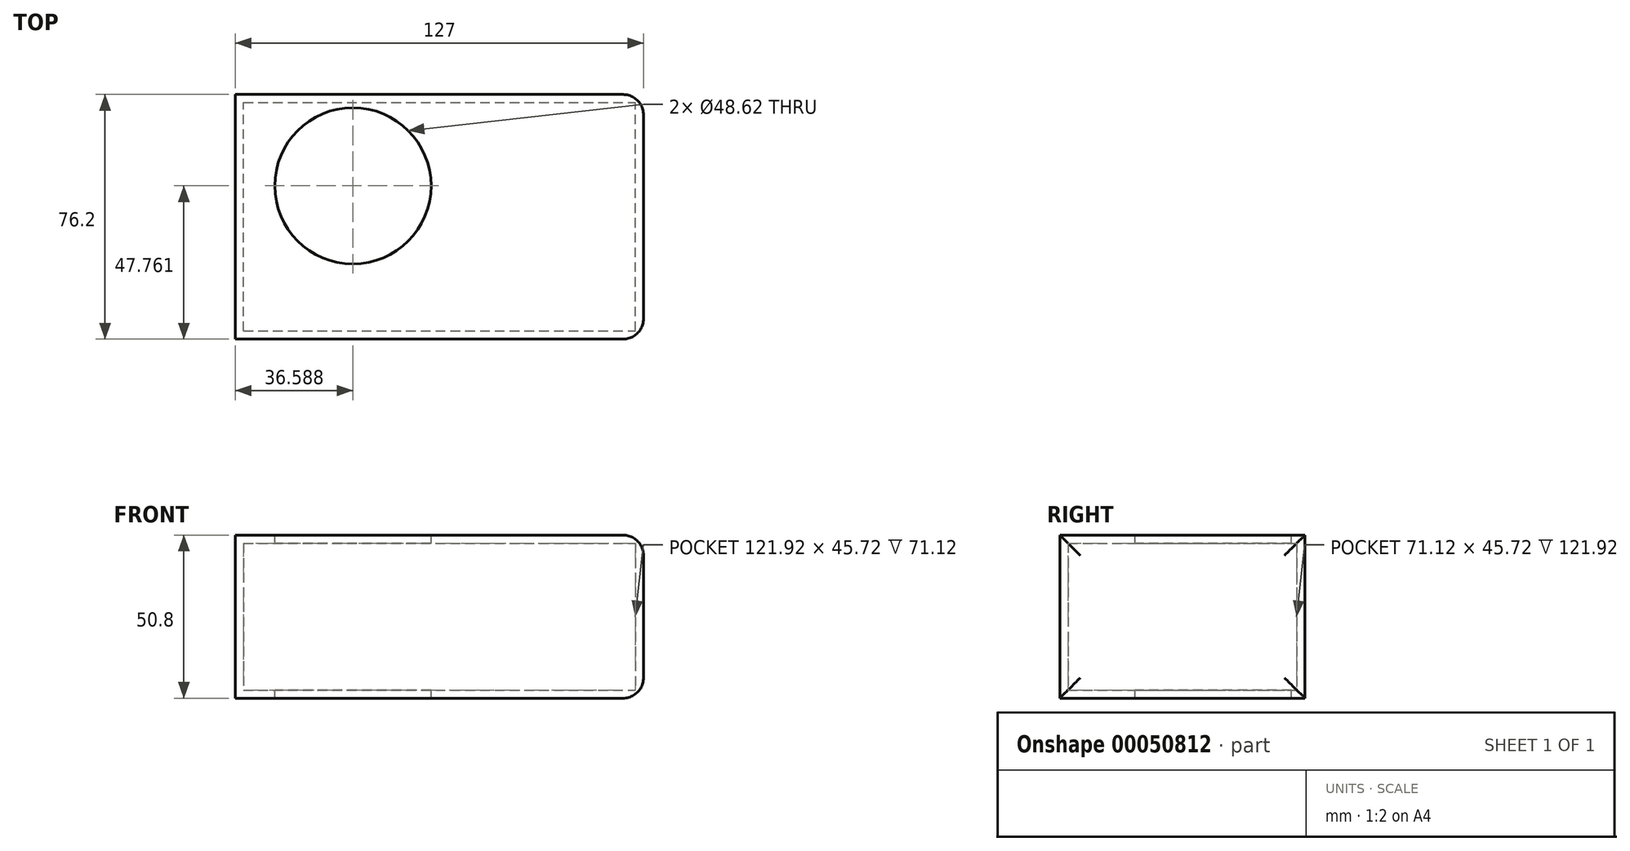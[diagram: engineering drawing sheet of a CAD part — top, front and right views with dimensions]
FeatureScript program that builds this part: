
annotation { "Feature Type Name" : "Feature", "Feature Type Description" : "" }
export const myFeature = defineFeature(function(context is Context, id is Id, definition is map)
    precondition{}
    {
        {
            var Q0;
            Q0=qCreatedBy(makeId("Top.planeOp"),FACE);
            var sketch = newSketch(context, id + "F0", { "sketchPlane" : qUnion([Q0])});
            skLineSegment(sketch, "E0.bottom", {"start": v(0, 0) * mm, "end": v(127, 0) * mm});
            skLineSegment(sketch, "E0.top", {"start": v(0, 76.2) * mm, "end": v(127, 76.2) * mm});
            skLineSegment(sketch, "E0.left", {"start": v(0, 0) * mm, "end": v(0, 76.2) * mm});
            skLineSegment(sketch, "E0.right", {"start": v(127, 0) * mm, "end": v(127, 76.2) * mm});
            skSolve(sketch);
        }
        {
            var Q0;
            Q0 = qSketchRegion(id + "F0", true);
            extrude(context, id + "F1", {"entities" : qUnion([Q0]), "depth" : 50.8 * mm});
        }
        {
            var Q0;
            Q0=makeQuery(id+"F1.opExtrude","CAP_FACE",FACE,{"disambiguationData":[OSD([sQuery(id+"F0.wireOp",EDGE,"E0.bottom"),sQuery(id+"F0.wireOp",EDGE,"E0.top"),sQuery(id+"F0.wireOp",EDGE,"E0.left"),sQuery(id+"F0.wireOp",EDGE,"E0.right")])],"isStart":false});
            var sketch = newSketch(context, id + "F2", { "sketchPlane" : qUnion([Q0])});
            skCircle(sketch, "E1", {"center": v(36.59, 47.76) * mm, "radius": 24.3 * mm});
            skSolve(sketch);
        }
        {
            var Q0;
            Q0 = qSketchRegion(id + "F2", true);
            extrude(context, id + "F3", {"entities" : qUnion([Q0]), "operationType" : NewBodyOperationType.REMOVE, "endBound" : BoundingType.THROUGH_ALL, "oppositeDirection" : true, "depth" : 25.4 * mm});
        }
        {
            var Q0;
            Q0=makeQuery(id+"F3.boolean.opBoolean","COPY",FACE,{"derivedFrom":makeQuery(id+"F3.opExtrude","SWEPT_FACE",FACE,{"disambiguationData":[OSD([sQuery(id+"F2.wireOp",EDGE,"E1")])]})});
            shell(context, id + "F4", {"entities" : qUnion([Q0]), "thickness" : 2.54 * mm});
        }
        {
            var Q0;
            Q0=makeQuery(id+"F1.opExtrude","SWEPT_EDGE",EDGE,{"disambiguationData":[OSD([sQuery(id+"F0.wireOp",EDGE,"E0.top"),sQuery(id+"F0.wireOp",EDGE,"E0.right")])]});
            var Q1;
            Q1=makeQuery(id+"F1.opExtrude","CAP_EDGE",EDGE,{"disambiguationData":[OSD([sQuery(id+"F0.wireOp",EDGE,"E0.right")])],"isStart":true});
            var Q2;
            Q2=makeQuery(id+"F1.opExtrude","SWEPT_EDGE",EDGE,{"disambiguationData":[OSD([sQuery(id+"F0.wireOp",EDGE,"E0.bottom"),sQuery(id+"F0.wireOp",EDGE,"E0.right")])]});
            var Q3;
            Q3=makeQuery(id+"F1.opExtrude","CAP_EDGE",EDGE,{"disambiguationData":[OSD([sQuery(id+"F0.wireOp",EDGE,"E0.right")])],"isStart":false});
            fillet(context, id + "F5", {"entities" : qUnion([Q0, Q1, Q2, Q3]), "radius" : 6.35 * mm, "tangentPropagation" : true, "allowEdgeOverflow" : false});
        }
    });
